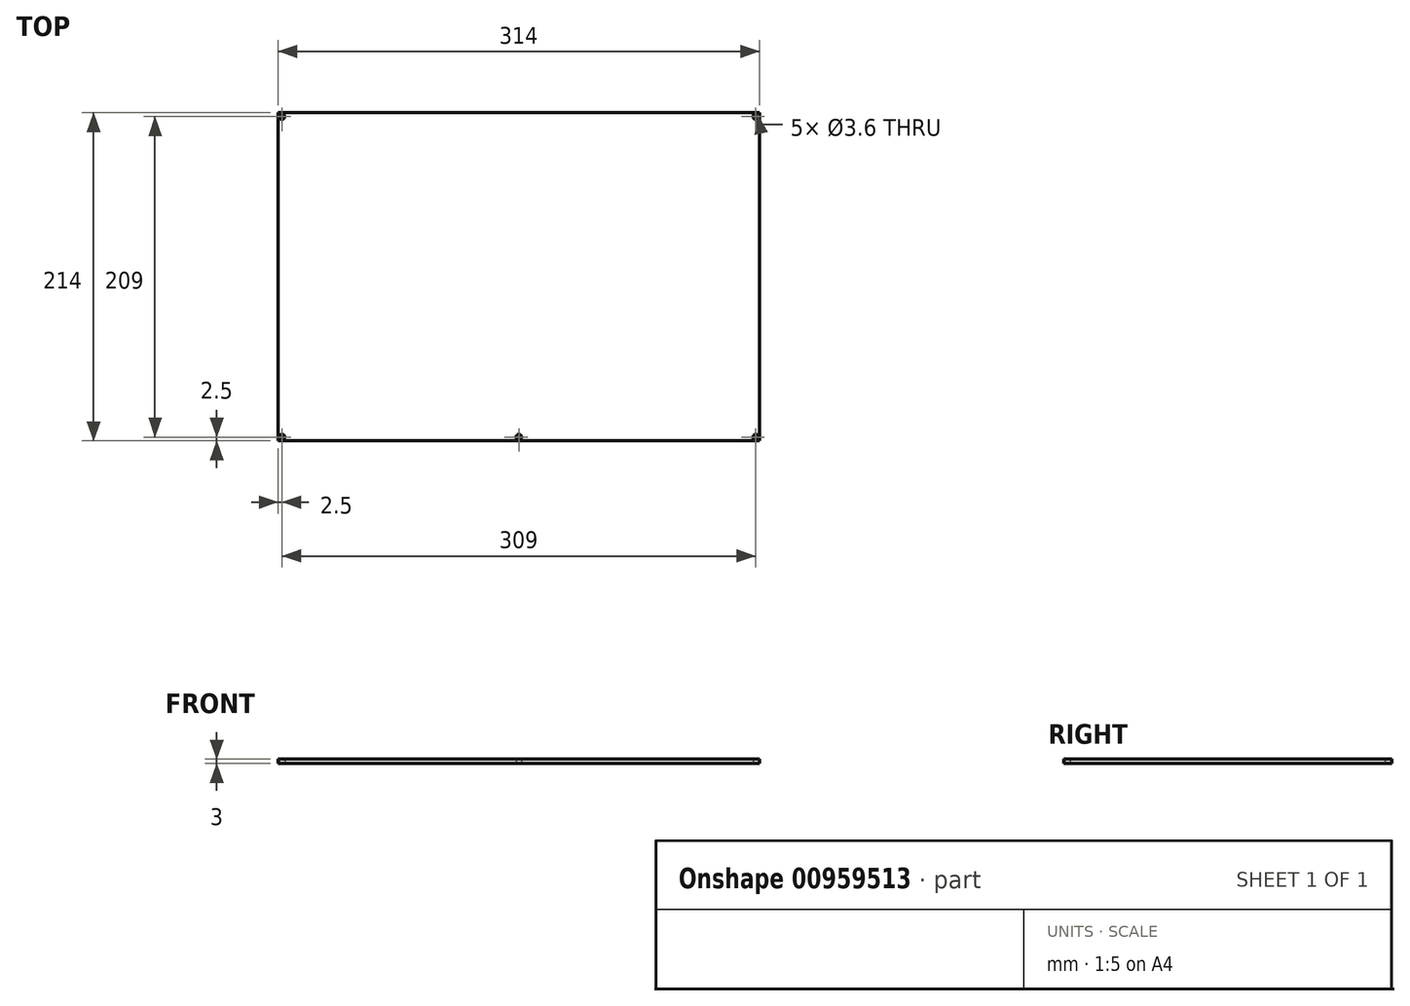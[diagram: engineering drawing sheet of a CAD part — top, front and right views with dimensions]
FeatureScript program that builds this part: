
annotation { "Feature Type Name" : "Feature", "Feature Type Description" : "" }
export const myFeature = defineFeature(function(context is Context, id is Id, definition is map)
    precondition{}
    {
        {
            var Q0;
            Q0=qCreatedBy(makeId("Top.planeOp"),FACE);
            var sketch = newSketch(context, id + "F0", { "sketchPlane" : qUnion([Q0])});
            skLineSegment(sketch, "E0.bottom", {"start": v(157, -107) * mm, "end": v(-157, -107) * mm});
            skLineSegment(sketch, "E0.top", {"start": v(157, 107) * mm, "end": v(-157, 107) * mm});
            skLineSegment(sketch, "E0.left", {"start": v(157, -107) * mm, "end": v(157, 107) * mm});
            skLineSegment(sketch, "E0.right", {"start": v(-157, -107) * mm, "end": v(-157, 107) * mm});
            skPoint(sketch, "E0.middle", {"position": v(0, 0) * mm});
            skLineSegment(sketch, "E1.bottom", {"start": v(154.5, -104.5) * mm, "end": v(-154.5, -104.5) * mm, "construction": true});
            skLineSegment(sketch, "E1.top", {"start": v(154.5, 104.5) * mm, "end": v(-154.5, 104.5) * mm, "construction": true});
            skLineSegment(sketch, "E1.left", {"start": v(154.5, -104.5) * mm, "end": v(154.5, 104.5) * mm, "construction": true});
            skLineSegment(sketch, "E1.right", {"start": v(-154.5, -104.5) * mm, "end": v(-154.5, 104.5) * mm, "construction": true});
            skCircle(sketch, "E2", {"center": v(-154.5, 104.5) * mm, "radius": 1.8 * mm});
            skCircle(sketch, "E3", {"center": v(154.5, 104.5) * mm, "radius": 1.8 * mm});
            skCircle(sketch, "E4", {"center": v(154.5, -104.5) * mm, "radius": 1.8 * mm});
            skCircle(sketch, "E5", {"center": v(-154.5, -104.5) * mm, "radius": 1.8 * mm});
            skPoint(sketch, "E6", {"position": v(0, -104.5) * mm});
            skCircle(sketch, "E7", {"center": v(0, -104.5) * mm, "radius": 1.8 * mm});
            skSolve(sketch);
        }
        {
            var Q0;
            Q0=makeQuery(id+"F0.imprint","IMPRINT",FACE,{"disambiguationData":[TD([[makeQuery(id+"F0.imprint","IMPRINT",EDGE,{"derivedFrom":sQuery(id+"F0.wireOp",EDGE,"E0.bottom")}),-1.0]])]});
            extrude(context, id + "F1", {"entities" : qUnion([Q0]), "depth" : 3 * mm, "offsetDistance" : 25 * mm});
        }
    });
